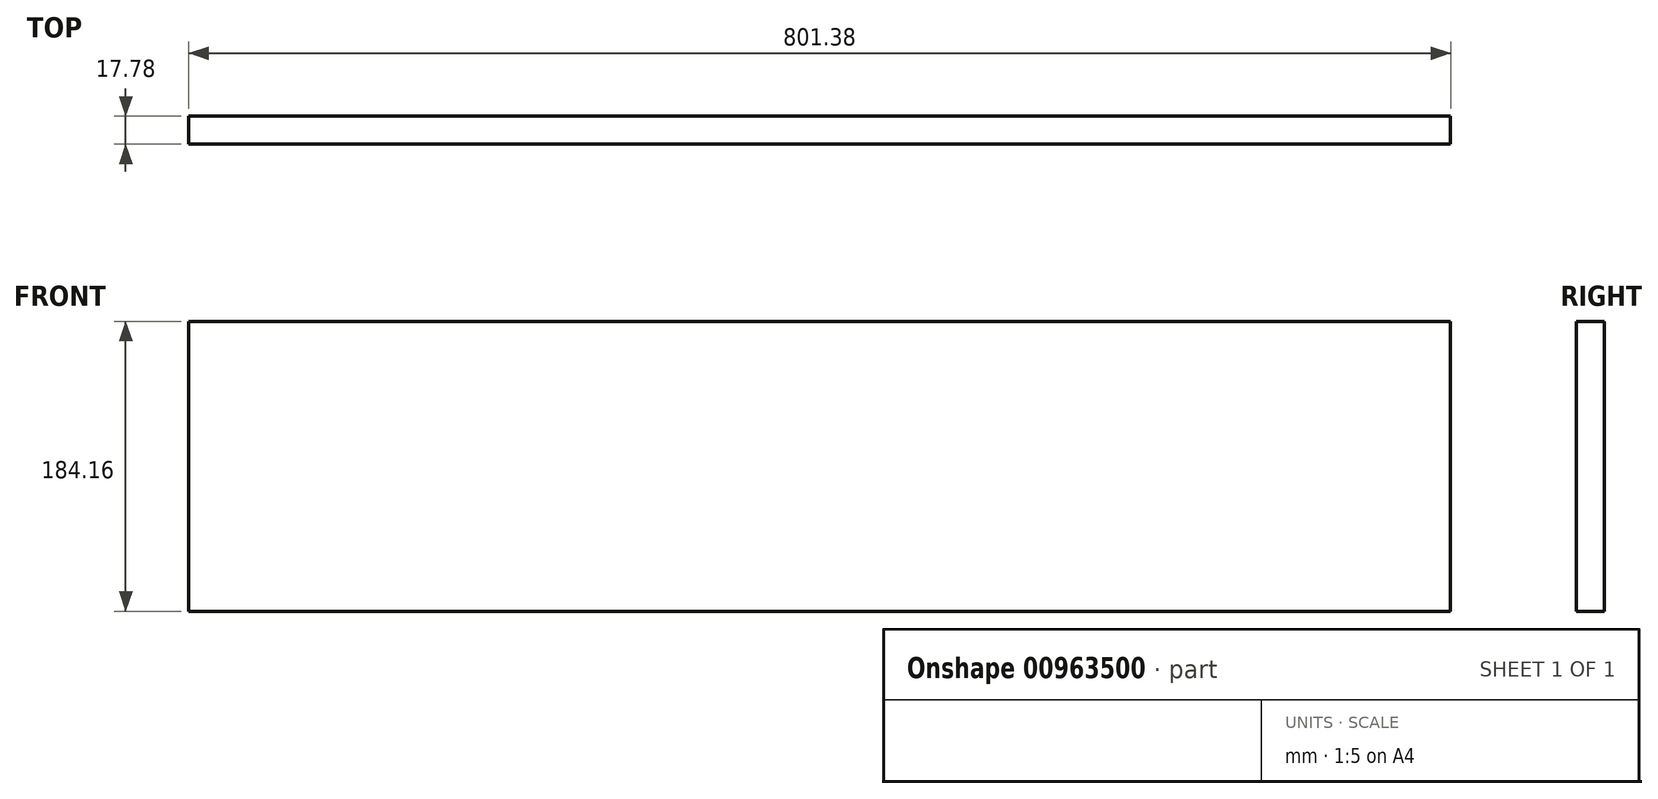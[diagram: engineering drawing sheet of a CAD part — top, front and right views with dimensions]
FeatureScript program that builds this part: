
annotation { "Feature Type Name" : "Feature", "Feature Type Description" : "" }
export const myFeature = defineFeature(function(context is Context, id is Id, definition is map)
    precondition{}
    {
        {
            var Q0;
            Q0=qCreatedBy(makeId("Front.planeOp"),FACE);
            var sketch = newSketch(context, id + "F0", { "sketchPlane" : qUnion([Q0])});
            skLineSegment(sketch, "E0.bottom", {"start": v(400.69, 92.08) * mm, "end": v(-400.69, 92.08) * mm});
            skLineSegment(sketch, "E0.top", {"start": v(400.69, -92.08) * mm, "end": v(-400.69, -92.08) * mm});
            skLineSegment(sketch, "E0.left", {"start": v(400.69, 92.08) * mm, "end": v(400.69, -92.08) * mm});
            skLineSegment(sketch, "E0.right", {"start": v(-400.69, 92.08) * mm, "end": v(-400.69, -92.08) * mm});
            skPoint(sketch, "E0.middle", {"position": v(0, 0) * mm});
            skSolve(sketch);
        }
        {
            var Q0;
            Q0=qSketchRegion(id+"F0",true);
            extrude(context, id + "F1", {"entities" : qUnion([Q0]), "depth" : 17.78 * mm, "offsetDistance" : 25.4 * mm});
        }
    });
